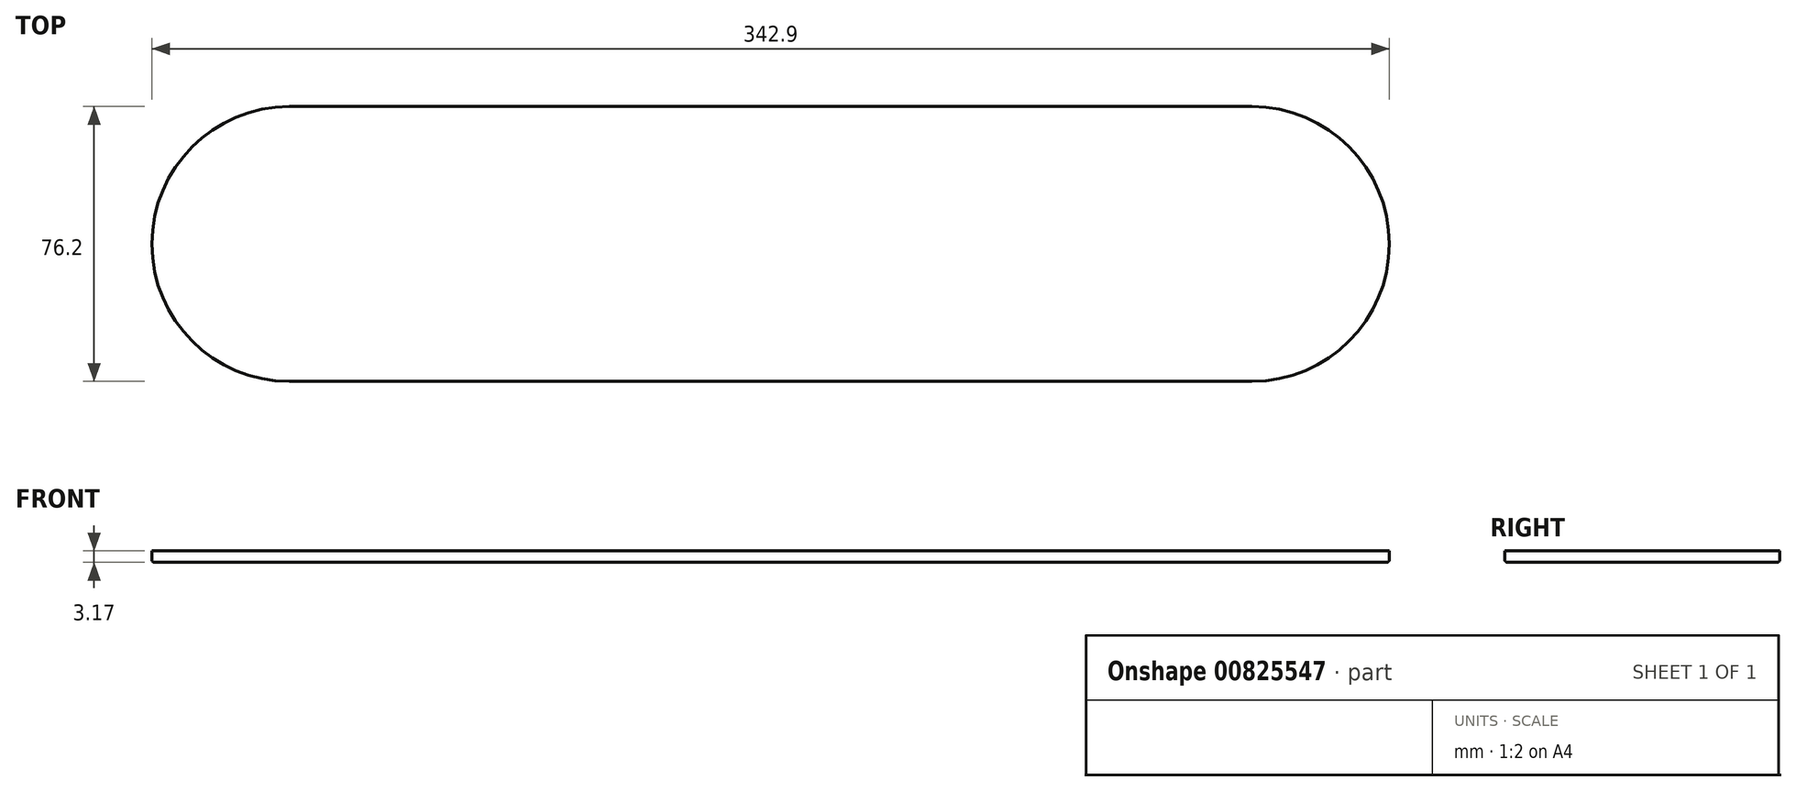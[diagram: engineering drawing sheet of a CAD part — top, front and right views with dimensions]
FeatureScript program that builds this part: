
annotation { "Feature Type Name" : "Feature", "Feature Type Description" : "" }
export const myFeature = defineFeature(function(context is Context, id is Id, definition is map)
    precondition{}
    {
        {
            var Q0;
            Q0=qCreatedBy(makeId("Top.planeOp"),FACE);
            var sketch = newSketch(context, id + "F0", { "sketchPlane" : qUnion([Q0])});
            skArc(sketch, "E0", {"start": v(0, 38.1) * mm, "mid": v(-38.1, 0) * mm, "end": v(0, -38.1) * mm});
            skArc(sketch, "E1", {"start": v(266.7, -38.1) * mm, "mid": v(304.8, 0) * mm, "end": v(266.7, 38.1) * mm});
            skLineSegment(sketch, "E2", {"start": v(0, 38.1) * mm, "end": v(266.7, 38.1) * mm});
            skLineSegment(sketch, "E3", {"start": v(266.7, -38.1) * mm, "end": v(0, -38.1) * mm});
            skSolve(sketch);
        }
        {
            var Q0;
            Q0=qSketchRegion(id+"F0",true);
            extrude(context, id + "F1", {"entities" : qUnion([Q0]), "depth" : 3.17 * mm, "offsetDistance" : 25.4 * mm});
        }
        {
            var Q0;
            Q0=makeQuery(id+"F1.opExtrude","CAP_FACE",FACE,{"disambiguationData":[OSD([sQuery(id+"F0.wireOp",EDGE,"E0"),sQuery(id+"F0.wireOp",EDGE,"E1"),sQuery(id+"F0.wireOp",EDGE,"E2"),sQuery(id+"F0.wireOp",EDGE,"E3")])],"isStart":true});
            fillet(context, id + "F2", {"entities" : qUnion([Q0]), "radius" : 0.8 * mm, "tangentPropagation" : true, "allowEdgeOverflow" : false});
        }
    });
